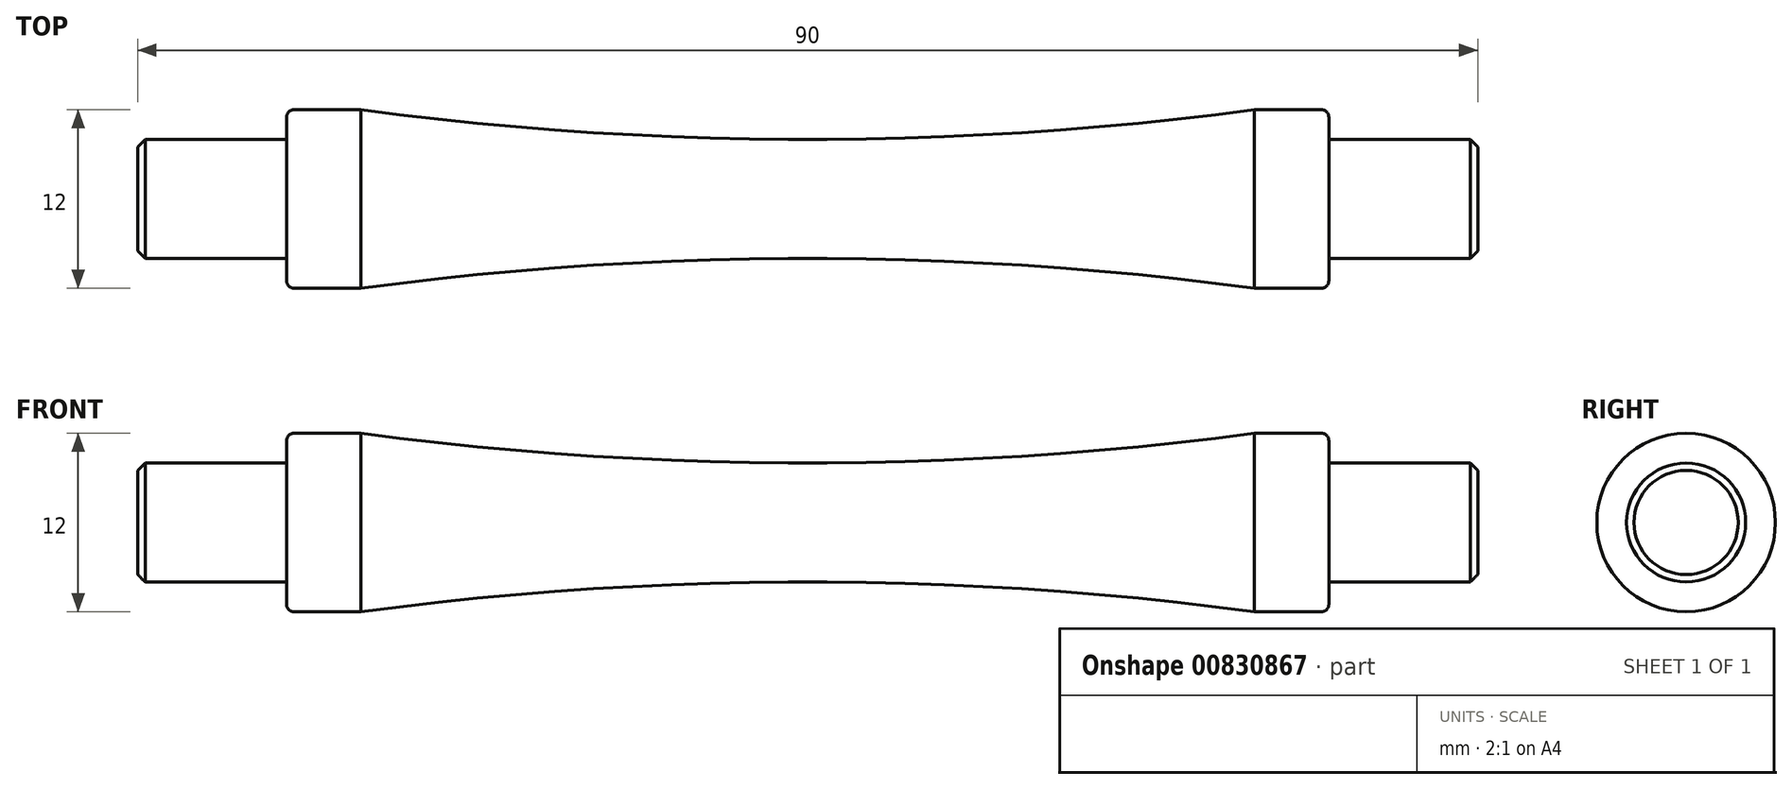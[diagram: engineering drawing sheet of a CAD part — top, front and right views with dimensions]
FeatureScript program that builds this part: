
annotation { "Feature Type Name" : "Feature", "Feature Type Description" : "" }
export const myFeature = defineFeature(function(context is Context, id is Id, definition is map)
    precondition{}
    {
        {
            var Q0;
            Q0=qCreatedBy(makeId("Right.planeOp"),FACE);
            var sketch = newSketch(context, id + "F0", { "sketchPlane" : qUnion([Q0])});
            skCircle(sketch, "E0", {"center": v(0, 0) * mm, "radius": 4 * mm});
            skSolve(sketch);
        }
        {
            var Q0;
            Q0 = qSketchRegion(id + "F0", true);
            extrude(context, id + "F1", {"entities" : qUnion([Q0]), "depth" : 90 * mm, "offsetDistance" : 25 * mm, "symmetric" : true});
        }
        {
            var Q0;
            Q0=qCreatedBy(makeId("Right.planeOp"),FACE);
            var sketch = newSketch(context, id + "F2", { "sketchPlane" : qUnion([Q0])});
            skCircle(sketch, "E1", {"center": v(0, 0) * mm, "radius": 6 * mm});
            skSolve(sketch);
        }
        {
            var Q0;
            Q0=makeQuery(id+"F2.imprint","IMPRINT",FACE,{"disambiguationData":[TD([[makeQuery(id+"F2.imprint","IMPRINT",EDGE,{"derivedFrom":sQuery(id+"F2.wireOp",EDGE,"E1")}),1.0]])]});
            extrude(context, id + "F3", {"entities" : qUnion([Q0]), "operationType" : NewBodyOperationType.ADD, "depth" : 70 * mm, "offsetDistance" : 25 * mm, "symmetric" : true});
        }
        {
            var Q0;
            Q0=qCreatedBy(makeId("Front.planeOp"),FACE);
            var sketch = newSketch(context, id + "F4", { "sketchPlane" : qUnion([Q0])});
            skLineSegment(sketch, "E2.bottom", {"start": v(-35, 6) * mm, "end": v(35, 6) * mm, "construction": true});
            skLineSegment(sketch, "E2.top", {"start": v(-35, -6) * mm, "end": v(35, -6) * mm, "construction": true});
            skLineSegment(sketch, "E2.left", {"start": v(-35, 6) * mm, "end": v(-35, -6) * mm, "construction": true});
            skLineSegment(sketch, "E2.right", {"start": v(35, 6) * mm, "end": v(35, -6) * mm, "construction": true});
            skPoint(sketch, "E2.middle", {"position": v(0, 0) * mm});
            skArc(sketch, "E3", {"start": v(-30, 6) * mm, "mid": v(0, 4) * mm, "end": v(30, 6) * mm});
            skLineSegment(sketch, "E4", {"start": v(-30, 6) * mm, "end": v(30, 6) * mm});
            skSolve(sketch);
        }
        {
            var Q0;
            Q0=qCreatedBy(makeId("Front.planeOp"),FACE);
            var sketch = newSketch(context, id + "F5", { "sketchPlane" : qUnion([Q0])});
            skLineSegment(sketch, "E5", {"start": v(0, 0) * mm, "end": v(25.17, 0) * mm});
            skSolve(sketch);
        }
        {
            var Q0;
            Q0 = qSketchRegion(id + "F4", true);
            var Q1;
            Q1=sQuery(id+"F5.wireOp",EDGE,"E5");
            revolve(context, id + "F6", {"operationType" : NewBodyOperationType.REMOVE, "surfaceOperationType" : NewSurfaceOperationType.NEW, "entities" : qUnion([Q0]), "axis" : qUnion([Q1]), "revolveType" : RevolveType.FULL, "oppositeDirection" : true});
        }
        {
            var Q0;
            Q0=makeQuery(id+"F3.opExtrude","CAP_EDGE",EDGE,{"disambiguationData":[OSD([sQuery(id+"F2.wireOp",EDGE,"E1")])],"isStart":true});
            var Q1;
            Q1=makeQuery(id+"F3.opExtrude","CAP_EDGE",EDGE,{"disambiguationData":[OSD([sQuery(id+"F2.wireOp",EDGE,"E1")])],"isStart":false});
            fillet(context, id + "F7", {"entities" : qUnion([Q0, Q1]), "radius" : 0.5 * mm, "tangentPropagation" : true, "allowEdgeOverflow" : false});
        }
        {
            var Q0;
            Q0=makeQuery(id+"F1.opExtrude","CAP_EDGE",EDGE,{"disambiguationData":[OSD([sQuery(id+"F0.wireOp",EDGE,"E0")])],"isStart":true});
            var Q1;
            Q1=makeQuery(id+"F1.opExtrude","CAP_EDGE",EDGE,{"disambiguationData":[OSD([sQuery(id+"F0.wireOp",EDGE,"E0")])],"isStart":false});
            chamfer(context, id + "F8", {"entities" : qUnion([Q0, Q1]), "width" : 0.5 * mm, "tangentPropagation" : true});
        }
    });
